# Revit family: Receptor_Sani_Flor_13-In_Square_6-In_Sump_Zurn-Z1755
name_source: partatom
category: Plumbing Fixtures
units: mm (PartAtom-declared; Revit-internal decimal feet)

## family parameters
Always vertical = Yes
Cut with Voids When Loaded = No
Maintain Annotation Orientation = No
OmniClass Number = 23.45.05.14.14
OmniClass Title = Sinks/Lavatories
Part Type = Normal
Room Calculation Point = No
Round Connector Dimension = Use Radius
Shared = No
Work Plane-Based = No

## types (6) — shared parameters
Approx. Weight (Lbs) = 10.000 lb
Assembly Code = D2030300
Body Height (E) = 8 "
Body Top SQ. Dimension = 13.375 "
CW Connection = No
Default Elevation = 20 "
Description = 13-3/8 [340] SQ. SANI-FLOR RECEPTOR 6 [152] SUMP W/ADJUSTABLE CLAMP FRAME
Grate Open Area (Sq.In.) = 25.000 in²
Grate Outer SQ. Dimension = 11.938 "
Grate SQ. Dimension = 9.875 "
HW Connection = No
Manufacturer = Zurn Water, LLC
Manufacurer Brand = Zurn
Model = Z1755
Modified Date = 01/23/2026
Product Documentation Link = https://files.zurn.com
Product Page URL = https://www.zurn.com
Product data url = https://www.bimobject.com
Sump Height = 6 "
URL = www.zurn.com
Vent Connection = No
WFU = 1
Waste Connection = Yes
zero-valued in all types: CWFU, HWFU

## per-type parameters (varying)
| type | Connector Radius | Main Material | Pipe Size_A Inside Diameter | Pipe Size_A Nominal Diameter | Pipe Size_A Outer Diameter |
| Z1755_2 Inch No-Hub | 1 " | Steel - Zurn - Stainless - Type - 304 | 2.067 " | 2 " | 2.375 " |
| Z1755_3 Inch No-Hub | 1.5 " | Steel - Zurn - Stainless - Type - 304 | 3.068 " | 3 " | 3.5 " |
| Z1755_4 Inch No-Hub | 2 " | Steel - Zurn - Stainless - Type - 304 | 4.026 " | 4 " | 4.5 " |
| ZM1755_2 Inch No-Hub | 1 " | Steel - Zurn - Stainless - Type - 316 | 2.067 " | 2 " | 2.375 " |
| ZM1755_3 Inch No-Hub | 1.5 " | Steel - Zurn - Stainless - Type - 316 | 3.068 " | 3 " | 3.5 " |
| ZM1755_4 Inch No-Hub | 2 " | Steel - Zurn - Stainless - Type - 316 | 4.026 " | 4 " | 4.5 " |

## geometry (parser evidence)
native form markers: Sweep x3
no freeform markers — native parametric forms only
